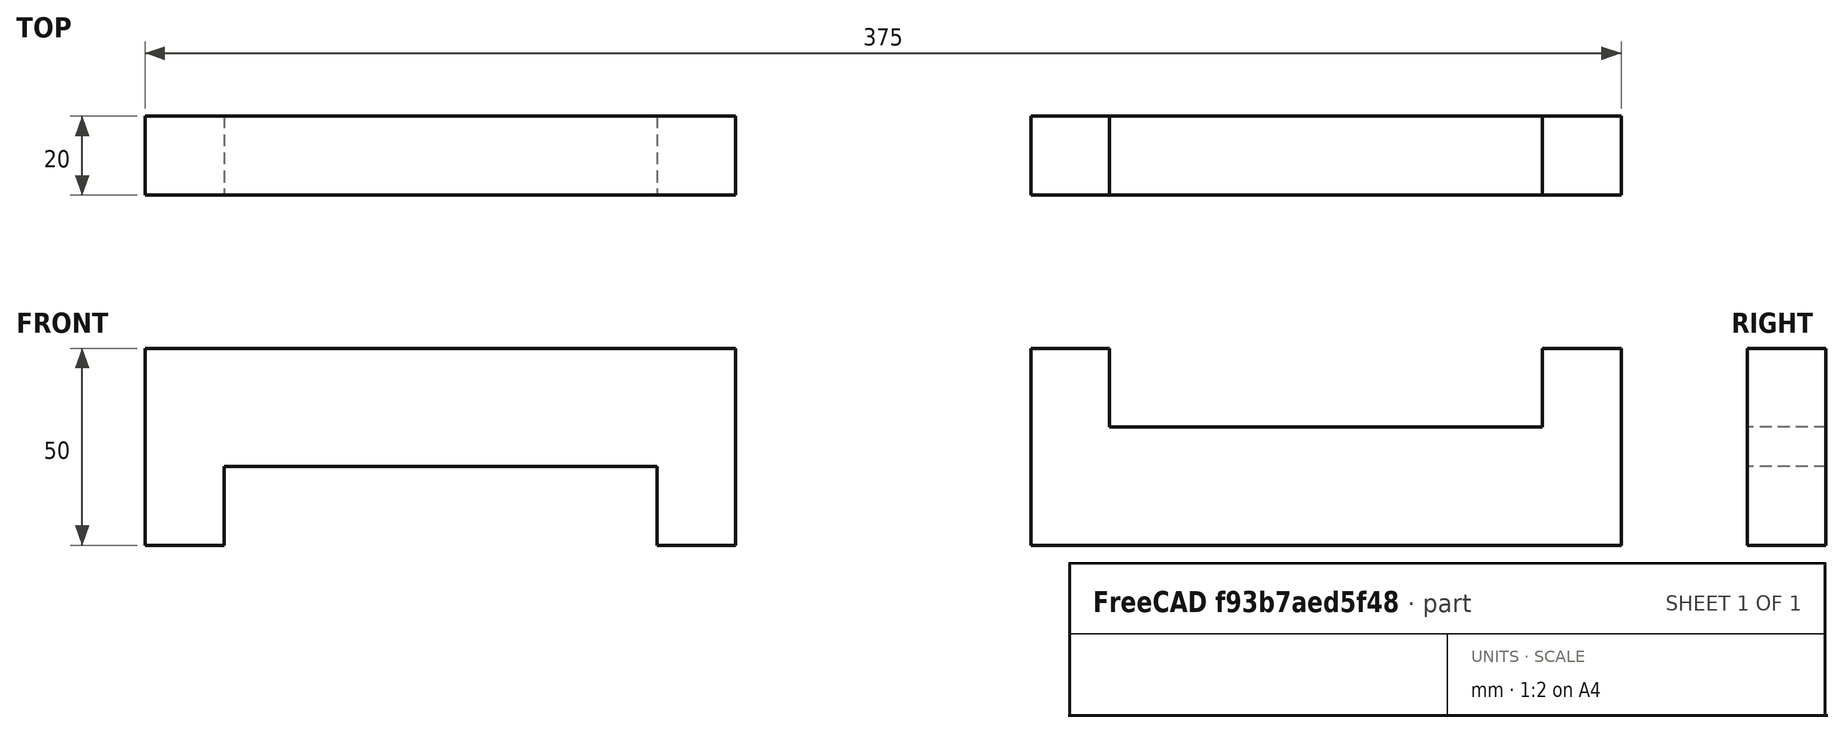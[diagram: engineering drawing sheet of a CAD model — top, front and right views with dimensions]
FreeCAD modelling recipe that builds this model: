
FCSTD DOCUMENT  (FreeCAD 0.16R6706 (Git))
Label: flat_surfaces
License: All rights reserved
LicenseURL: http://en.wikipedia.org/wiki/All_rights_reserved
objects: Sketcher::SketchObject×1, PartDesign::Pad×1, Drawing::FeatureViewPart×1, Drawing::FeaturePage×1
note: 3 computed .brp shape members not serialized (recipe doc carries the construction recipe); baked Part::Feature solids carry a one-line shape summary decoded from their .brp

FEATURE [Sketcher::SketchObject] Sketch
  Placement = pos=(0,0,0) rot=(-1,0,0;4.71239rad)
  sketch-geometry (16):
    g0: LineSegment StartX=0 StartY=50 StartZ=0 EndX=0 EndY=0 EndZ=0
    g1: LineSegment StartX=0 StartY=0 StartZ=0 EndX=20 EndY=0 EndZ=0
    g2: LineSegment StartX=20 StartY=0 StartZ=0 EndX=20 EndY=20 EndZ=0
    g3: LineSegment StartX=20 StartY=20 StartZ=0 EndX=130 EndY=20 EndZ=0
    g4: LineSegment StartX=130 StartY=20 StartZ=0 EndX=130 EndY=0 EndZ=0
    g5: LineSegment StartX=130 StartY=0 StartZ=0 EndX=150 EndY=0 EndZ=0
    g6: LineSegment StartX=150 StartY=0 StartZ=0 EndX=150 EndY=50 EndZ=0
    g7: LineSegment StartX=150 StartY=50 StartZ=0 EndX=0 EndY=50 EndZ=0
    g8: LineSegment StartX=225 StartY=50 StartZ=0 EndX=225 EndY=0 EndZ=0
    g9: LineSegment StartX=225 StartY=0 StartZ=0 EndX=375 EndY=0 EndZ=0
    g10: LineSegment StartX=375 StartY=0 StartZ=0 EndX=375 EndY=50 EndZ=0
    g11: LineSegment StartX=375 StartY=50 StartZ=0 EndX=355 EndY=50 EndZ=0
    g12: LineSegment StartX=355 StartY=50 StartZ=0 EndX=355 EndY=30 EndZ=0
    g13: LineSegment StartX=355 StartY=30 StartZ=0 EndX=245 EndY=30 EndZ=0
    g14: LineSegment StartX=245 StartY=30 StartZ=0 EndX=245 EndY=50 EndZ=0
    g15: LineSegment StartX=245 StartY=50 StartZ=0 EndX=225 EndY=50 EndZ=0
  constraints (49):
    c: Vertical(g0)
    c: Coincident(g0,g1)
    c: Horizontal(g1)
    c: Coincident(g1,g2)
    c: Vertical(g2)
    c: Coincident(g2,g3)
    c: Coincident(g3,g4)
    c: Vertical(g4)
    c: Coincident(g4,g5)
    c: Horizontal(g5)
    c: Coincident(g5,g6)
    c: Vertical(g6)
    c: Coincident(g6,g7)
    c: Coincident(g7,g0)
    c: Horizontal(g7)
    c: PointOnObject(g1,g-1)
    c: PointOnObject(g4,g-1)
    c: Equal(g1,g5)
    c: DistanceY(g0,g0) = 50
    c: DistanceY(g2,g2) = 20
    c: DistanceX(g1,g1) = 20
    c: DistanceX(g7,g7) = 150
    c: Coincident(g0,g-1)
    c: PointOnObject(g8,g-1)
    c: Vertical(g8)
    c: Coincident(g8,g9)
    c: Horizontal(g9)
    c: Coincident(g9,g10)
    c: Vertical(g10)
    c: Coincident(g10,g11)
    c: Horizontal(g11)
    c: Coincident(g11,g12)
    c: Vertical(g12)
    c: Coincident(g12,g13)
    c: Horizontal(g13)
    c: Coincident(g13,g14)
    c: Vertical(g14)
    c: Coincident(g14,g15)
    c: Coincident(g15,g8)
    c: Horizontal(g15)
    c: Equal(g15,g11)
    c: Equal(g11,g5)
    c: Equal(g8,g6)
    c: Equal(g13,g3)
    c: Equal(g9,g7)
    c: DistanceX(g5,g8) = 75
    c: Equal(g14,g2)
    c: Equal(g10,g8)
    c: Equal(g7,g9)
FEATURE [PartDesign::Pad] Pad
  Length = 20
  Length2 = 100
  Placement = pos=(0,0,0) rot=(-1,0,0;4.71239rad)
  Sketch = -> Sketch
  Type = 0
FEATURE [Drawing::FeatureViewPart] View
  Direction = (0,-1,0)
  HiddenWidth = 0.15
  LineWidth = 0.35
  Rotation = 90
  Scale = 0.25
  ShowHiddenLines = false
  ShowSmoothLines = false
  Source = -> Pad
  Tolerance = 0.05
  ViewResult = <g id="View"\n   transform="rotate(90,58.125,154.75) translate(58.125,154.75) scale(0.25,0.25)"\n  >\n<g   stroke="rgb(0, 0, 0)"\n   stroke-width="1.4"\n   stroke-linecap="butt"\n   stroke-linejoin="miter"\n   fill="none"\n   transform="scale(1,-1)"\n  >\n<path id= "1" d=" M -50 225 L 7.10543e-15 225 " />\n<path id= "2" d=" M -8.88178e-15 225 L -8.88178e-15 375 " />\n<path id= "3" d=" M -8.88178e-15 375 L -50 375 " />\n<path id= "4" d=" M -50 375 L -50 355 " />\n<path id= "5" d=" M -50 355 L -30 355 " />\n<path id= "6" d=" M -30 355 L -30 245 " />\n<path id= "7" d=" M -30 245 L -50 245 " />\n<path id= "8" d=" M -50 245 L -50 225 " />\n<path id= "9" d=" M -50 0 L 7.10543e-15 0 " />\n<path id= "10" d=" M -8.88178e-15 0 L -8.88178e-15 20 " />\n<path id= "11" d=" M -8.88178e-15 20 L -20 20 " />\n<path id= "12" d=" M -20 20 L -20 130 " />\n<path id= "13" d=" M -20 130 L -3.55271e-15 130 " />\n<path id= "14" d=" M -8.88178e-15 130 L -8.88178e-15 150 " />\n<path id= "15" d=" M -8.88178e-15 150 L -50 150 " />\n<path id= "16" d=" M -50 150 L -50 -2.84217e-14 " />\n</g>\n</g>
  Visible = true
  X = 58.125
  Y = 154.75
FEATURE [Drawing::FeaturePage] Page
  Group = -> [View]
